# Revit family: P200921MX-019c_MER8800FZ
name_source: partatom
category: Specialty Equipment
units: mm (PartAtom-declared; Revit-internal decimal feet)

## family parameters
Always vertical = Yes
Cut with Voids When Loaded = No
Enable Cutting in Views = No
Maintain Annotation Orientation = No
Part Type = Normal
Room Calculation Point = No
Round Connector Dimension = Use Diameter
Shared = No
Work Plane-Based = No

## types (1)
- MER8800FZ
    Amps = 0 A
    Back Panel Material = ARCAT - Metal - Aluminum
    Body Material = ARCAT - Metal - Steel - Black
    Clearance Material = ARCAT - Clearance
    Cooktop Material = ARCAT - Glass - Black
    Default Elevation = 0"
    Depth = 27 3/4"
    Description = 30-Inch Wide Electric Range With True Convection And Power Preheat - 6.4 Cu. Ft.
    Dimension Guide = http://access.whirlpool.com Guide&sku=MER8800FZ&language=EN
    Display Panel Material = ARCAT - Glass - Black Light
    Door Material = ARCAT - Metal - Steel - Stainless
    Family Name = Cooking
    Feature 1 = Fingerprint Resistant Stainless Steel
    Feature 2 = True Convection with Third Element
    Feature 3 = Precision Cooking™ System
    Glass Material = ARCAT - Glass - Tempered - Black
    Handle Material = ARCAT - Metal - Steel -Gray Light
    Height = 47 7/8"
    Installation-Fabrication = https://www.whirlpool.com
    Knob Material = ARCAT - Metal - Steel -Gray Light
    Leg Material = ARCAT - Plastic - Black
    Manufacturer = Maytag
    Model = MER8800FZ
    Voltage = 0 V
    Width = 29 7/8"

## geometry (parser evidence)
native form markers: Sweep x5
no freeform markers — native parametric forms only
